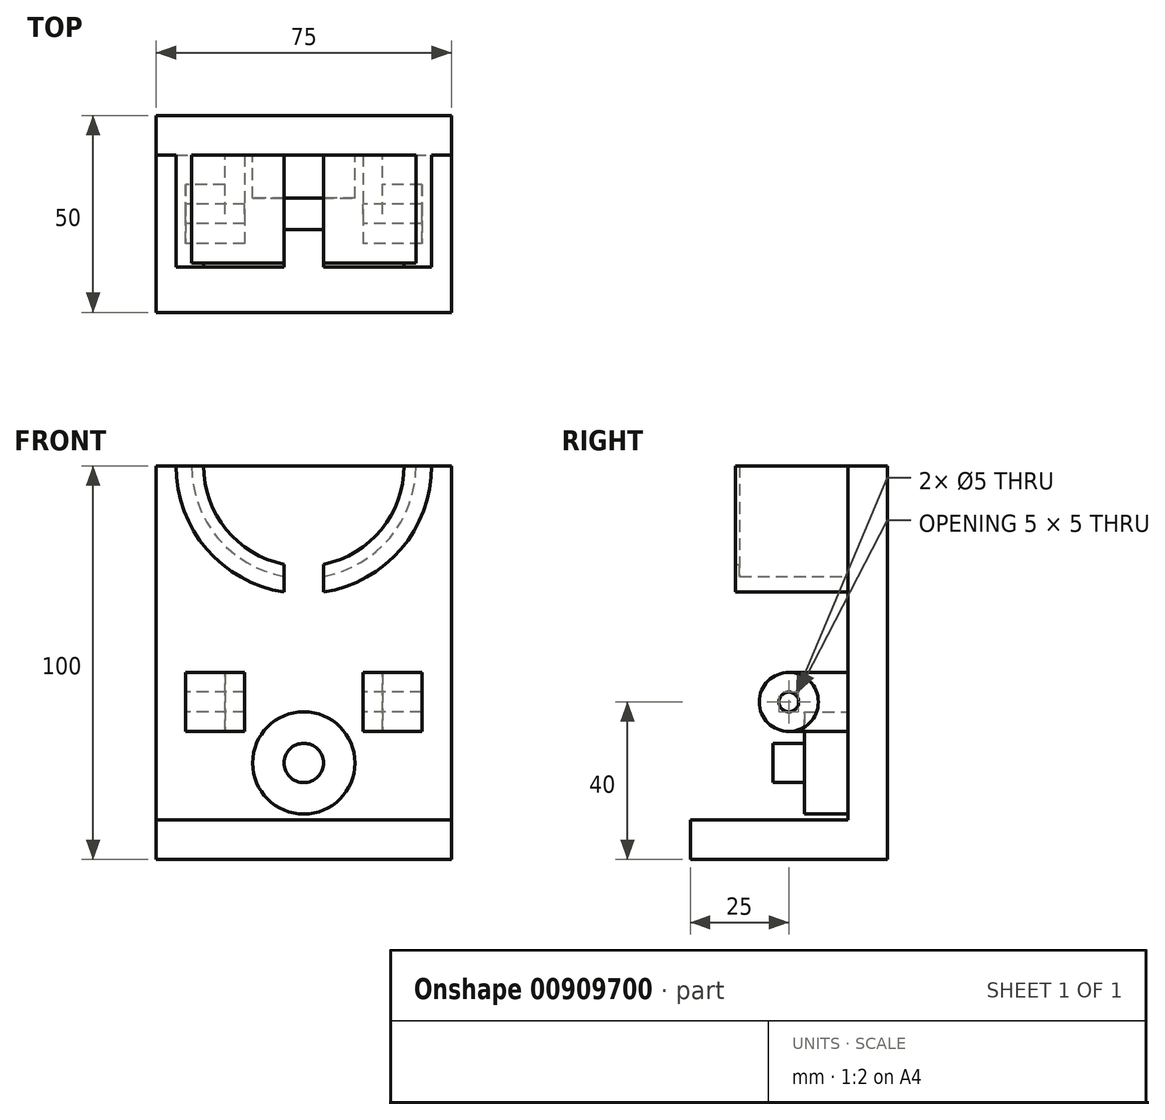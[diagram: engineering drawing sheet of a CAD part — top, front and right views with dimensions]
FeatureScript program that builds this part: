
annotation { "Feature Type Name" : "Feature", "Feature Type Description" : "" }
export const myFeature = defineFeature(function(context is Context, id is Id, definition is map)
    precondition{}
    {
        {
            var Q0;
            Q0=qCreatedBy(makeId("Front.planeOp"),FACE);
            var sketch = newSketch(context, id + "F0", { "sketchPlane" : qUnion([Q0])});
            skCircle(sketch, "E0", {"center": v(0, 100) * mm, "radius": 28.5 * mm});
            skLineSegment(sketch, "E1.top", {"start": v(20, 100) * mm, "end": v(-20, 100) * mm});
            skLineSegment(sketch, "E2.bottom", {"start": v(-37.5, 0) * mm, "end": v(37.5, 0) * mm});
            skLineSegment(sketch, "E2.top", {"start": v(-37.5, 100) * mm, "end": v(37.5, 100) * mm});
            skLineSegment(sketch, "E2.left", {"start": v(-37.5, 0) * mm, "end": v(-37.5, 100) * mm});
            skLineSegment(sketch, "E2.right", {"start": v(37.5, 0) * mm, "end": v(37.5, 100) * mm});
            skSolve(sketch);
        }
        {
            var Q0;
            Q0=makeQuery(id+"F0.imprint","IMPRINT",FACE,{"disambiguationData":[TD([[makeQuery(id+"F0.imprint","IMPRINT",EDGE,{"derivedFrom":sQuery(id+"F0.wireOp",EDGE,"E2.bottom")}),1.0]])]});
            var Q1;
            {var subQ4=sQuery(id+"F0.wireOp",EDGE,"E1.top");Q1=makeQuery(id+"F0.imprint","IMPRINT",FACE,{"disambiguationData":[TD([[makeQuery(id+"F0.imprint","IMPRINT",EDGE,{"derivedFrom":subQ4}),1.0]])]});}
            extrude(context, id + "F1", {"entities" : qUnion([Q0, Q1]), "depth" : 10 * mm, "offsetDistance" : 25 * mm});
        }
        {
            var Q0;
            Q0=makeQuery(id+"F1.opExtrude","CAP_FACE",FACE,{"disambiguationData":[OSD([sQuery(id+"F0.wireOp",EDGE,"E1.top"),sQuery(id+"F0.wireOp",EDGE,"E2.bottom"),sQuery(id+"F0.wireOp",EDGE,"E2.top"),sQuery(id+"F0.wireOp",EDGE,"E2.left"),sQuery(id+"F0.wireOp",EDGE,"E2.right")])],"isStart":false});
            var sketch = newSketch(context, id + "F2", { "sketchPlane" : qUnion([Q0])});
            skLineSegment(sketch, "E3.bottom", {"start": v(-37.5, 0) * mm, "end": v(37.5, 0) * mm});
            skLineSegment(sketch, "E3.top", {"start": v(-37.5, 10) * mm, "end": v(37.5, 10) * mm});
            skLineSegment(sketch, "E3.left", {"start": v(-37.5, 0) * mm, "end": v(-37.5, 10) * mm});
            skLineSegment(sketch, "E3.right", {"start": v(37.5, 0) * mm, "end": v(37.5, 10) * mm});
            skSolve(sketch);
        }
        {
            var Q0;
            Q0 = qSketchRegion(id + "F2", true);
            extrude(context, id + "F3", {"entities" : qUnion([Q0]), "operationType" : NewBodyOperationType.ADD, "depth" : 40 * mm, "offsetDistance" : 25 * mm});
        }
        {
            var Q0;
            Q0=makeQuery(id+"F1.opExtrude","CAP_FACE",FACE,{"disambiguationData":[OSD([sQuery(id+"F0.wireOp",EDGE,"E1.top"),sQuery(id+"F0.wireOp",EDGE,"E2.bottom"),sQuery(id+"F0.wireOp",EDGE,"E2.top"),sQuery(id+"F0.wireOp",EDGE,"E2.left"),sQuery(id+"F0.wireOp",EDGE,"E2.right")])],"isStart":false});
            var sketch = newSketch(context, id + "F4", { "sketchPlane" : qUnion([Q0])});
            skLineSegment(sketch, "E4.bottom", {"start": v(20, 32.5) * mm, "end": v(-20, 32.5) * mm});
            skLineSegment(sketch, "E4.top", {"start": v(20, 47.5) * mm, "end": v(-20, 47.5) * mm});
            skLineSegment(sketch, "E4.left", {"start": v(20, 32.5) * mm, "end": v(20, 47.5) * mm});
            skLineSegment(sketch, "E4.right", {"start": v(-20, 32.5) * mm, "end": v(-20, 47.5) * mm});
            skPoint(sketch, "E4.middle", {"position": v(0, 40) * mm});
            skSolve(sketch);
        }
        {
            var Q0;
            Q0 = qSketchRegion(id + "F4", true);
            var Q1;
            Q1 = qSketchRegion(id + "FjxjfPKiOoM7iHV_1", true);
            extrude(context, id + "F5", {"entities" : qUnion([Q0, Q1]), "operationType" : NewBodyOperationType.ADD, "depth" : 15 * mm, "offsetDistance" : 25 * mm});
        }
        {
            var Q0;
            Q0=makeQuery(id+"F5.opExtrude","SWEPT_FACE",FACE,{"disambiguationData":[OSD([sQuery(id+"F4.wireOp",EDGE,"E4.right")])]});
            var sketch = newSketch(context, id + "F6", { "sketchPlane" : qUnion([Q0])});
            skCircle(sketch, "E5", {"center": v(25, 40) * mm, "radius": 7.5 * mm});
            skSolve(sketch);
        }
        {
            var Q0;
            {var subQ1=sQuery(id+"F4.wireOp",EDGE,"E4.right");var subQ2=makeQuery(id+"F5.opExtrude","CAP_EDGE",EDGE,{"disambiguationData":[OSD([subQ1])],"isStart":false});Q0=makeQuery(id+"F6.imprint","IMPRINT",FACE,{"disambiguationData":[TD([[makeQuery(id+"F6.imprint","IMPRINT",EDGE,{"derivedFrom":subQ2}),-1.0]])]});}
            var Q1;
            {var subQ1=sQuery(id+"F4.wireOp",EDGE,"E4.right");var subQ2=makeQuery(id+"F5.opExtrude","CAP_EDGE",EDGE,{"disambiguationData":[OSD([subQ1])],"isStart":false});Q1=makeQuery(id+"F6.imprint","IMPRINT",FACE,{"disambiguationData":[TD([[makeQuery(id+"F6.imprint","IMPRINT",EDGE,{"derivedFrom":subQ2}),1.0]])]});}
            extrude(context, id + "F7", {"entities" : qUnion([Q0, Q1]), "operationType" : NewBodyOperationType.ADD, "depth" : -40 * mm, "offsetDistance" : 25 * mm});
        }
        {
            var Q0;
            Q0=makeQuery(id+"F7.boolean.opBoolean","MERGE",FACE,{"derivedFrom":[makeQuery(id+"F5.opExtrude","SWEPT_FACE",FACE,{"disambiguationData":[OSD([sQuery(id+"F4.wireOp",EDGE,"E4.right")])]}),makeQuery(id+"F7.opExtrude","CAP_FACE",FACE,{"disambiguationData":[OSD([sQuery(id+"F6.wireOp",EDGE,"E5")])],"isStart":true})]});
            var sketch = newSketch(context, id + "F8", { "sketchPlane" : qUnion([Q0])});
            skCircle(sketch, "E6", {"center": v(25, 40) * mm, "radius": 2.5 * mm});
            skSolve(sketch);
        }
        {
            var Q0;
            Q0 = qSketchRegion(id + "F8", true);
            extrude(context, id + "F9", {"entities" : qUnion([Q0]), "depth" : -40 * mm, "offsetDistance" : 25 * mm});
        }
        {
            var Q0;
            Q0=makeQuery(id+"F9.opExtrude","SWEPT_BODY",BODY,{"disambiguationData":[OSD([sQuery(id+"F8.wireOp",EDGE,"E6")])]});
            var Q1;
            Q1=makeQuery(id+"F1.opExtrude","SWEPT_BODY",BODY,{"disambiguationData":[OSD([sQuery(id+"F0.wireOp",EDGE,"E1.top"),sQuery(id+"F0.wireOp",EDGE,"E2.bottom"),sQuery(id+"F0.wireOp",EDGE,"E2.top"),sQuery(id+"F0.wireOp",EDGE,"E2.left"),sQuery(id+"F0.wireOp",EDGE,"E2.right")])]});
            booleanBodies(context, id + "F10", {"operationType" : BooleanOperationType.SUBTRACTION, "tools" : qUnion([Q0]), "targets" : qUnion([Q1])});
        }
        {
            var Q0;
            Q0=makeQuery(id+"F1.opExtrude","CAP_FACE",FACE,{"disambiguationData":[OSD([sQuery(id+"F0.wireOp",EDGE,"E1.top"),sQuery(id+"F0.wireOp",EDGE,"E2.bottom"),sQuery(id+"F0.wireOp",EDGE,"E2.top"),sQuery(id+"F0.wireOp",EDGE,"E2.left"),sQuery(id+"F0.wireOp",EDGE,"E2.right")])],"isStart":false});
            var sketch = newSketch(context, id + "F11", { "sketchPlane" : qUnion([Q0])});
            skLineSegment(sketch, "E7.bottom", {"start": v(15, 52.5) * mm, "end": v(-15, 52.5) * mm});
            skLineSegment(sketch, "E7.top", {"start": v(15, 27.5) * mm, "end": v(-15, 27.5) * mm});
            skLineSegment(sketch, "E7.left", {"start": v(15, 52.5) * mm, "end": v(15, 27.5) * mm});
            skLineSegment(sketch, "E7.right", {"start": v(-15, 52.5) * mm, "end": v(-15, 27.5) * mm});
            skPoint(sketch, "E7.middle", {"position": v(0, 40) * mm});
            skSolve(sketch);
        }
        {
            var Q0;
            Q0 = qSketchRegion(id + "F11", true);
            extrude(context, id + "F12", {"entities" : qUnion([Q0]), "depth" : 50 * mm, "offsetDistance" : 25 * mm});
        }
        {
            var Q0;
            Q0=makeQuery(id+"F12.opExtrude","SWEPT_BODY",BODY,{"disambiguationData":[OSD([sQuery(id+"F11.wireOp",EDGE,"E7.bottom"),sQuery(id+"F11.wireOp",EDGE,"E7.top"),sQuery(id+"F11.wireOp",EDGE,"E7.left"),sQuery(id+"F11.wireOp",EDGE,"E7.right")])]});
            var Q1;
            Q1=makeQuery(id+"F1.opExtrude","SWEPT_BODY",BODY,{"disambiguationData":[OSD([sQuery(id+"F0.wireOp",EDGE,"E1.top"),sQuery(id+"F0.wireOp",EDGE,"E2.bottom"),sQuery(id+"F0.wireOp",EDGE,"E2.top"),sQuery(id+"F0.wireOp",EDGE,"E2.left"),sQuery(id+"F0.wireOp",EDGE,"E2.right")])]});
            booleanBodies(context, id + "F13", {"operationType" : BooleanOperationType.SUBTRACTION, "tools" : qUnion([Q0]), "targets" : qUnion([Q1])});
        }
        {
            var Q0;
            Q0=makeQuery(id+"F13.opBoolean","MERGE",FACE,{"derivedFrom":[makeQuery(id+"F1.opExtrude","CAP_FACE",FACE,{"disambiguationData":[OSD([sQuery(id+"F0.wireOp",EDGE,"E1.top"),sQuery(id+"F0.wireOp",EDGE,"E2.bottom"),sQuery(id+"F0.wireOp",EDGE,"E2.top"),sQuery(id+"F0.wireOp",EDGE,"E2.left"),sQuery(id+"F0.wireOp",EDGE,"E2.right")])],"isStart":false})],"fromTools":[makeQuery(id+"F12.opExtrude","CAP_FACE",FACE,{"disambiguationData":[OSD([sQuery(id+"F11.wireOp",EDGE,"E7.bottom"),sQuery(id+"F11.wireOp",EDGE,"E7.top"),sQuery(id+"F11.wireOp",EDGE,"E7.left"),sQuery(id+"F11.wireOp",EDGE,"E7.right")])],"isStart":true})]});
            var sketch = newSketch(context, id + "F14", { "sketchPlane" : qUnion([Q0])});
            skCircle(sketch, "E8", {"center": v(0, 24.5) * mm, "radius": 13 * mm});
            skPoint(sketch, "E8.centerSnap0", {"position": v(15, 24.5) * mm});
            skSolve(sketch);
        }
        {
            var Q0;
            Q0=makeQuery(id+"F14.imprint","IMPRINT",FACE,{"disambiguationData":[TD([[makeQuery(id+"F14.imprint","IMPRINT",EDGE,{"derivedFrom":sQuery(id+"F14.wireOp",EDGE,"E8")}),1.0]])]});
            extrude(context, id + "F15", {"entities" : qUnion([Q0]), "operationType" : NewBodyOperationType.ADD, "depth" : 11 * mm, "offsetDistance" : 25 * mm});
        }
        {
            var Q0;
            Q0=makeQuery(id+"F15.opExtrude","CAP_FACE",FACE,{"disambiguationData":[OSD([sQuery(id+"F14.wireOp",EDGE,"E8")])],"isStart":false});
            var sketch = newSketch(context, id + "F16", { "sketchPlane" : qUnion([Q0])});
            skCircle(sketch, "E9", {"center": v(0, 24.5) * mm, "radius": 5 * mm});
            skSolve(sketch);
        }
        {
            var Q0;
            Q0 = qSketchRegion(id + "F16", true);
            extrude(context, id + "F17", {"entities" : qUnion([Q0]), "operationType" : NewBodyOperationType.ADD, "depth" : 8 * mm, "offsetDistance" : 25 * mm});
        }
        {
            var Q0;
            Q0=makeQuery(id+"F13.opBoolean","MERGE",FACE,{"derivedFrom":[makeQuery(id+"F1.opExtrude","CAP_FACE",FACE,{"disambiguationData":[OSD([sQuery(id+"F0.wireOp",EDGE,"E1.top"),sQuery(id+"F0.wireOp",EDGE,"E2.bottom"),sQuery(id+"F0.wireOp",EDGE,"E2.top"),sQuery(id+"F0.wireOp",EDGE,"E2.left"),sQuery(id+"F0.wireOp",EDGE,"E2.right")])],"isStart":false})],"fromTools":[makeQuery(id+"F12.opExtrude","CAP_FACE",FACE,{"disambiguationData":[OSD([sQuery(id+"F11.wireOp",EDGE,"E7.bottom"),sQuery(id+"F11.wireOp",EDGE,"E7.top"),sQuery(id+"F11.wireOp",EDGE,"E7.left"),sQuery(id+"F11.wireOp",EDGE,"E7.right")])],"isStart":true})]});
            var sketch = newSketch(context, id + "F18", { "sketchPlane" : qUnion([Q0])});
            skCircle(sketch, "E10", {"center": v(0, 100) * mm, "radius": 28.5 * mm});
            skArc(sketch, "E11", {"start": v(-28.5, 100) * mm, "mid": v(0, 71.5) * mm, "end": v(28.5, 100) * mm});
            skArc(sketch, "E12", {"start": v(-32.5, 100) * mm, "mid": v(0, 67.5) * mm, "end": v(32.5, 100) * mm});
            skLineSegment(sketch, "E13", {"start": v(-32.5, 100) * mm, "end": v(-28.5, 100) * mm});
            skLineSegment(sketch, "E14", {"start": v(28.5, 100) * mm, "end": v(32.5, 100) * mm});
            skSolve(sketch);
        }
        {
            var Q0;
            Q0=makeQuery(id+"F18.imprint","IMPRINT",FACE,{"disambiguationData":[TD([[makeQuery(id+"F18.imprint","IMPRINT",EDGE,{"derivedFrom":sQuery(id+"F18.wireOp",EDGE,"E11")}),-1.0]])]});
            extrude(context, id + "F19", {"entities" : qUnion([Q0]), "operationType" : NewBodyOperationType.ADD, "depth" : 27.5 * mm, "offsetDistance" : 25 * mm});
        }
        {
            var Q0;
            Q0=makeQuery(id+"F19.opExtrude","CAP_FACE",FACE,{"disambiguationData":[OSD([sQuery(id+"F18.wireOp",EDGE,"E11"),sQuery(id+"F18.wireOp",EDGE,"E12"),sQuery(id+"F18.wireOp",EDGE,"E13"),sQuery(id+"F18.wireOp",EDGE,"E14")])],"isStart":false});
            var sketch = newSketch(context, id + "F20", { "sketchPlane" : qUnion([Q0])});
            skCircle(sketch, "E15", {"center": v(0, 100) * mm, "radius": 28.5 * mm});
            skLineSegment(sketch, "E16.top", {"start": v(20, 100) * mm, "end": v(-20, 100) * mm});
            skLineSegment(sketch, "E17.bottom", {"start": v(-37.5, 0) * mm, "end": v(37.5, 0) * mm});
            skLineSegment(sketch, "E17.top", {"start": v(-37.5, 100) * mm, "end": v(37.5, 100) * mm});
            skLineSegment(sketch, "E17.left", {"start": v(-37.5, 0) * mm, "end": v(-37.5, 100) * mm});
            skLineSegment(sketch, "E17.right", {"start": v(37.5, 0) * mm, "end": v(37.5, 100) * mm});
            skArc(sketch, "E18", {"start": v(-25.5, 100) * mm, "mid": v(0, 74.5) * mm, "end": v(25.5, 100) * mm});
            skLineSegment(sketch, "E19", {"start": v(-32.5, 100) * mm, "end": v(-25.5, 100) * mm});
            skLineSegment(sketch, "E20", {"start": v(25.5, 100) * mm, "end": v(32.5, 100) * mm});
            skSolve(sketch);
        }
        {
            var Q0;
            {var subQ4=sQuery(id+"F20.wireOp",EDGE,"E18");Q0=makeQuery(id+"F20.imprint","IMPRINT",FACE,{"disambiguationData":[TD([[makeQuery(id+"F20.imprint","IMPRINT",EDGE,{"derivedFrom":subQ4}),-1.0]])]});}
            var Q1;
            {var subQ4=makeQuery(id+"F19.opExtrude","CAP_EDGE",EDGE,{"disambiguationData":[OSD([sQuery(id+"F18.wireOp",EDGE,"E12")])],"isStart":false});Q1=makeQuery(id+"F20.imprint","IMPRINT",FACE,{"disambiguationData":[TD([[makeQuery(id+"F20.imprint","IMPRINT",EDGE,{"derivedFrom":subQ4}),1.0]])]});}
            extrude(context, id + "F21", {"entities" : qUnion([Q0, Q1]), "operationType" : NewBodyOperationType.ADD, "depth" : 1 * mm, "offsetDistance" : 25 * mm});
        }
        {
            var Q0;
            {var subQ0=sQuery(id+"F0.wireOp",EDGE,"E2.top");var subQ1=sQuery(id+"F0.wireOp",EDGE,"E1.top");Q0=makeQuery(id+"F19.boolean.opBoolean","SPLIT",FACE,{"disambiguationData":[TD([makeQuery(id+"F19.opExtrude","SWEPT_FACE",FACE,{"disambiguationData":[OSD([sQuery(id+"F18.wireOp",EDGE,"E11")])]})])],"derivedFrom":makeQuery(id+"F13.opBoolean","MERGE",FACE,{"derivedFrom":[makeQuery(id+"F1.opExtrude","CAP_FACE",FACE,{"disambiguationData":[OSD([subQ1,sQuery(id+"F0.wireOp",EDGE,"E2.bottom"),subQ0,sQuery(id+"F0.wireOp",EDGE,"E2.left"),sQuery(id+"F0.wireOp",EDGE,"E2.right")])],"isStart":false})],"fromTools":[makeQuery(id+"F12.opExtrude","CAP_FACE",FACE,{"disambiguationData":[OSD([sQuery(id+"F11.wireOp",EDGE,"E7.bottom"),sQuery(id+"F11.wireOp",EDGE,"E7.top"),sQuery(id+"F11.wireOp",EDGE,"E7.left"),sQuery(id+"F11.wireOp",EDGE,"E7.right")])],"isStart":true})]})});}
            var sketch = newSketch(context, id + "F22", { "sketchPlane" : qUnion([Q0])});
            skLineSegment(sketch, "E21.bottom", {"start": v(5, 81.3) * mm, "end": v(-5, 81.3) * mm});
            skLineSegment(sketch, "E21.top", {"start": v(5, 56.7) * mm, "end": v(-5, 56.7) * mm});
            skLineSegment(sketch, "E21.left", {"start": v(5, 81.3) * mm, "end": v(5, 56.7) * mm});
            skLineSegment(sketch, "E21.right", {"start": v(-5, 81.3) * mm, "end": v(-5, 56.7) * mm});
            skPoint(sketch, "E21.middle", {"position": v(0, 69) * mm});
            skSolve(sketch);
        }
        {
            var Q0;
            Q0 = qSketchRegion(id + "F22", true);
            extrude(context, id + "F23", {"entities" : qUnion([Q0]), "depth" : 50 * mm, "offsetDistance" : 25 * mm});
        }
        {
            var Q0;
            Q0=makeQuery(id+"F23.opExtrude","SWEPT_BODY",BODY,{"disambiguationData":[OSD([sQuery(id+"F22.wireOp",EDGE,"E21.bottom"),sQuery(id+"F22.wireOp",EDGE,"E21.top"),sQuery(id+"F22.wireOp",EDGE,"E21.left"),sQuery(id+"F22.wireOp",EDGE,"E21.right")])]});
            var Q1;
            Q1=makeQuery(id+"F1.opExtrude","SWEPT_BODY",BODY,{"disambiguationData":[OSD([sQuery(id+"F0.wireOp",EDGE,"E1.top"),sQuery(id+"F0.wireOp",EDGE,"E2.bottom"),sQuery(id+"F0.wireOp",EDGE,"E2.top"),sQuery(id+"F0.wireOp",EDGE,"E2.left"),sQuery(id+"F0.wireOp",EDGE,"E2.right")])]});
            booleanBodies(context, id + "F24", {"operationType" : BooleanOperationType.SUBTRACTION, "tools" : qUnion([Q0]), "targets" : qUnion([Q1])});
        }
        {
            var Q0;
            Q0=makeQuery(id+"F7.boolean.opBoolean","MERGE",FACE,{"derivedFrom":[makeQuery(id+"F5.opExtrude","SWEPT_FACE",FACE,{"disambiguationData":[OSD([sQuery(id+"F4.wireOp",EDGE,"E4.right")])]}),makeQuery(id+"F7.opExtrude","CAP_FACE",FACE,{"disambiguationData":[OSD([sQuery(id+"F6.wireOp",EDGE,"E5")])],"isStart":true})]});
            var sketch = newSketch(context, id + "F25", { "sketchPlane" : qUnion([Q0])});
            skCircle(sketch, "E22", {"center": v(25, 40) * mm, "radius": 2.5 * mm});
            skCircle(sketch, "E23", {"center": v(25, 40) * mm, "radius": 7.5 * mm});
            skSolve(sketch);
        }
        {
            var Q0;
            Q0 = qSketchRegion(id + "F25", true);
            extrude(context, id + "F26", {"entities" : qUnion([Q0]), "operationType" : NewBodyOperationType.ADD, "depth" : 10 * mm, "offsetDistance" : 25 * mm});
        }
        {
            var Q0;
            Q0=makeQuery(id+"F7.boolean.opBoolean","MERGE",FACE,{"derivedFrom":[makeQuery(id+"F5.opExtrude","SWEPT_FACE",FACE,{"disambiguationData":[OSD([sQuery(id+"F4.wireOp",EDGE,"E4.left")])]}),makeQuery(id+"F7.opExtrude","CAP_FACE",FACE,{"disambiguationData":[OSD([sQuery(id+"F6.wireOp",EDGE,"E5")])],"isStart":false})]});
            var sketch = newSketch(context, id + "F27", { "sketchPlane" : qUnion([Q0])});
            skCircle(sketch, "E24", {"center": v(-25, 40) * mm, "radius": 2.5 * mm});
            skCircle(sketch, "E25", {"center": v(-25, 40) * mm, "radius": 7.5 * mm});
            skSolve(sketch);
        }
        {
            var Q0;
            Q0 = qSketchRegion(id + "F27", true);
            extrude(context, id + "F28", {"entities" : qUnion([Q0]), "operationType" : NewBodyOperationType.ADD, "depth" : 10 * mm, "offsetDistance" : 25 * mm});
        }
    });
